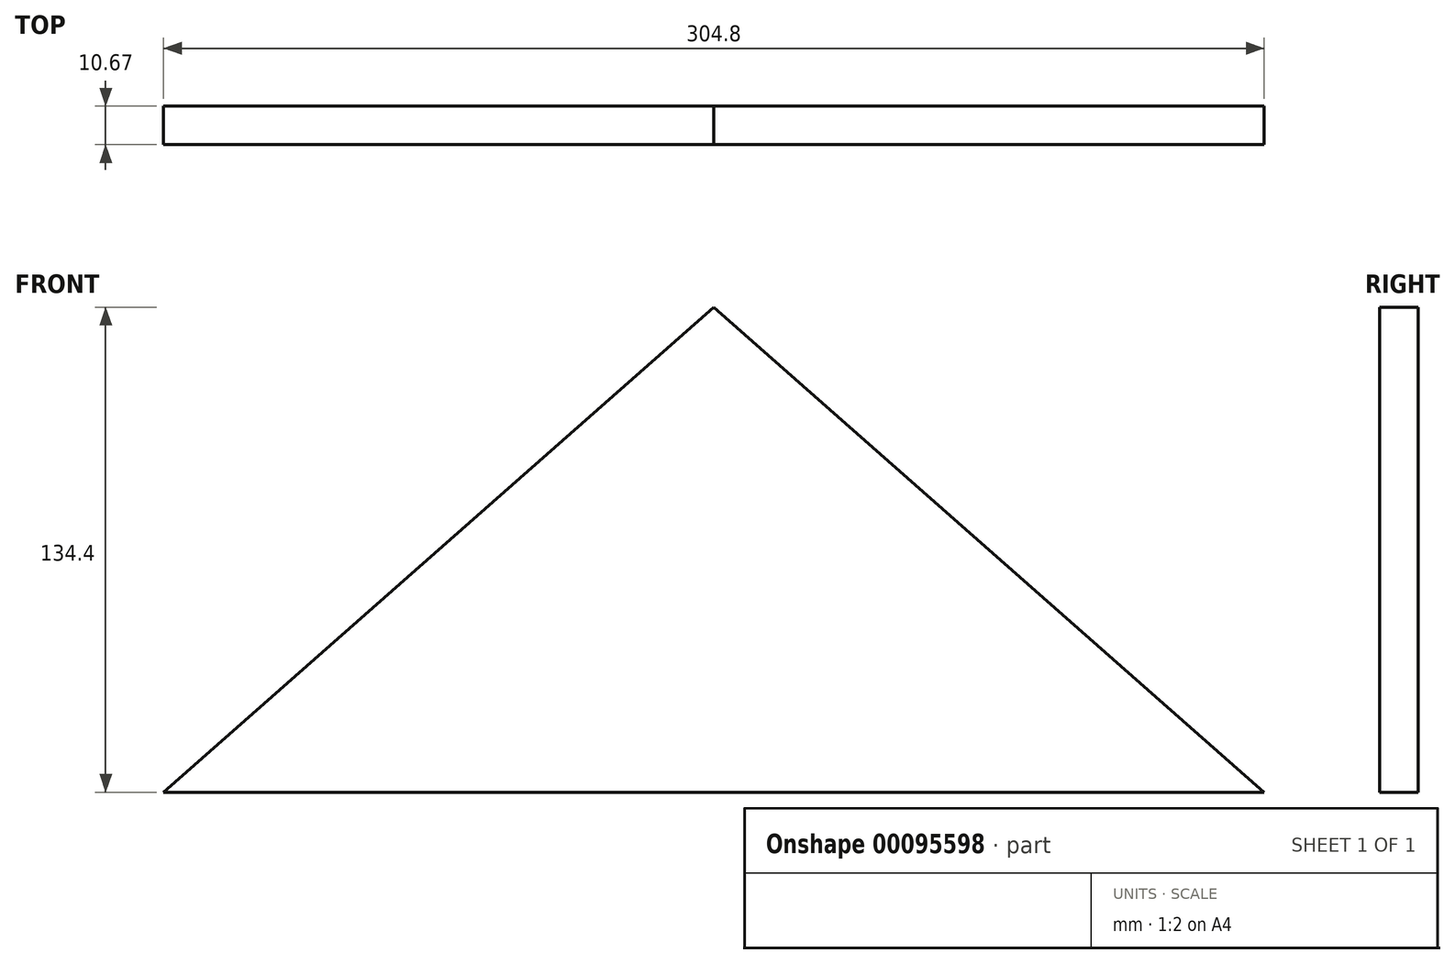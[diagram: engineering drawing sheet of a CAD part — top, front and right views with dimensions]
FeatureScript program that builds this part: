
annotation { "Feature Type Name" : "Feature", "Feature Type Description" : "" }
export const myFeature = defineFeature(function(context is Context, id is Id, definition is map)
    precondition{}
    {
        {
            var Q0;
            Q0=qCreatedBy(makeId("Front.planeOp"),FACE);
            var sketch = newSketch(context, id + "F0", { "sketchPlane" : qUnion([Q0])});
            skLineSegment(sketch, "E0", {"start": v(0, 134.4) * mm, "end": v(-152.4, 0) * mm});
            skLineSegment(sketch, "E1", {"start": v(-152.4, 0) * mm, "end": v(152.4, 0) * mm});
            skLineSegment(sketch, "E2", {"start": v(152.4, 0) * mm, "end": v(0, 134.4) * mm});
            skSolve(sketch);
        }
        {
            var Q0;
            Q0 = qSketchRegion(id + "F0", true);
            extrude(context, id + "F1", {"entities" : qUnion([Q0]), "depth" : 10.67 * mm});
        }
    });
